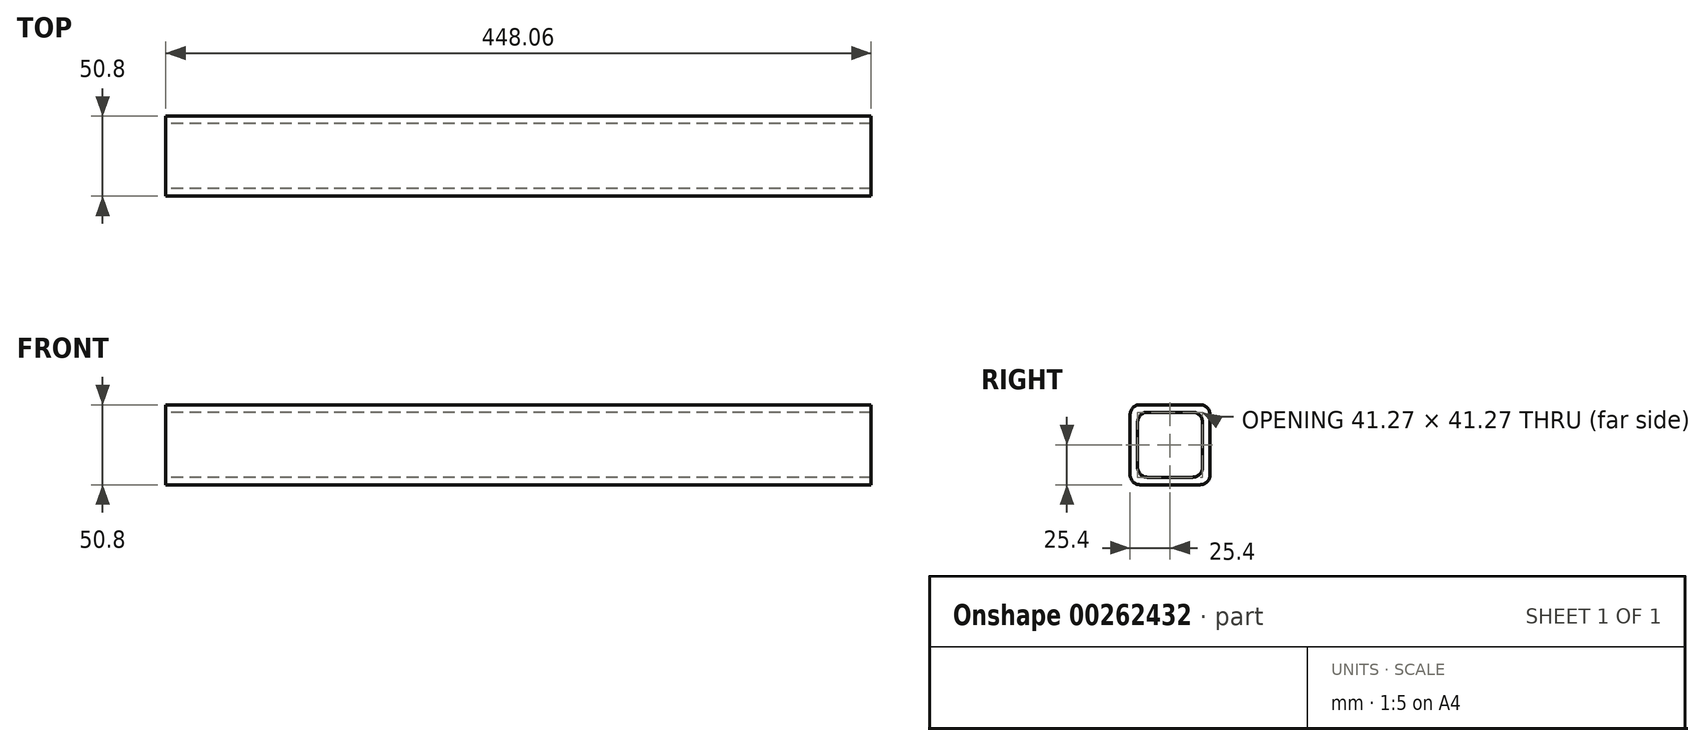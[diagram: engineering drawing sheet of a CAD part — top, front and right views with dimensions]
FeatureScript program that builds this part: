
annotation { "Feature Type Name" : "Feature", "Feature Type Description" : "" }
export const myFeature = defineFeature(function(context is Context, id is Id, definition is map)
    precondition{}
    {
        {
            var Q0;
            Q0=qCreatedBy(makeId("Right.planeOp"),FACE);
            var sketch = newSketch(context, id + "F0", { "sketchPlane" : qUnion([Q0])});
            skLineSegment(sketch, "E0.bottom", {"start": v(19.05, 25.4) * mm, "end": v(-19.05, 25.4) * mm});
            skLineSegment(sketch, "E0.top", {"start": v(19.05, -25.4) * mm, "end": v(-19.05, -25.4) * mm});
            skLineSegment(sketch, "E0.left", {"start": v(25.4, 19.05) * mm, "end": v(25.4, -19.05) * mm});
            skLineSegment(sketch, "E0.right", {"start": v(-25.4, 19.05) * mm, "end": v(-25.4, -19.05) * mm});
            skPoint(sketch, "E0.middle", {"position": v(0, 0) * mm});
            skLineSegment(sketch, "E1.bottom", {"start": v(14.29, 20.64) * mm, "end": v(-14.29, 20.64) * mm});
            skLineSegment(sketch, "E1.top", {"start": v(14.29, -20.64) * mm, "end": v(-14.29, -20.64) * mm});
            skLineSegment(sketch, "E1.left", {"start": v(20.64, 14.29) * mm, "end": v(20.64, -14.29) * mm});
            skLineSegment(sketch, "E1.right", {"start": v(-20.64, 14.29) * mm, "end": v(-20.64, -14.29) * mm});
            skPoint(sketch, "E2.visualSharp", {"position": v(-25.4, 25.4) * mm});
            skArc(sketch, "E2.filletArc", {"start": v(-19.05, 25.4) * mm, "mid": v(-23.54, 23.54) * mm, "end": v(-25.4, 19.05) * mm});
            skPoint(sketch, "E3.visualSharp", {"position": v(-20.64, 20.64) * mm});
            skArc(sketch, "E3.filletArc", {"start": v(-14.29, 20.64) * mm, "mid": v(-18.78, 18.78) * mm, "end": v(-20.64, 14.29) * mm});
            skPoint(sketch, "E4.visualSharp", {"position": v(-25.4, -25.4) * mm});
            skArc(sketch, "E4.filletArc", {"start": v(-25.4, -19.05) * mm, "mid": v(-23.54, -23.54) * mm, "end": v(-19.05, -25.4) * mm});
            skPoint(sketch, "E5.visualSharp", {"position": v(-20.64, -20.64) * mm});
            skArc(sketch, "E5.filletArc", {"start": v(-20.64, -14.29) * mm, "mid": v(-18.78, -18.78) * mm, "end": v(-14.29, -20.64) * mm});
            skPoint(sketch, "E6.visualSharp", {"position": v(20.64, 20.64) * mm});
            skArc(sketch, "E6.filletArc", {"start": v(20.64, 14.29) * mm, "mid": v(18.78, 18.78) * mm, "end": v(14.29, 20.64) * mm});
            skPoint(sketch, "E7.visualSharp", {"position": v(25.4, 25.4) * mm});
            skArc(sketch, "E7.filletArc", {"start": v(25.4, 19.05) * mm, "mid": v(23.54, 23.54) * mm, "end": v(19.05, 25.4) * mm});
            skPoint(sketch, "E8.visualSharp", {"position": v(20.64, -20.64) * mm});
            skArc(sketch, "E8.filletArc", {"start": v(14.29, -20.64) * mm, "mid": v(18.78, -18.78) * mm, "end": v(20.64, -14.29) * mm});
            skPoint(sketch, "E9.visualSharp", {"position": v(25.4, -25.4) * mm});
            skArc(sketch, "E9.filletArc", {"start": v(19.05, -25.4) * mm, "mid": v(23.54, -23.54) * mm, "end": v(25.4, -19.05) * mm});
            skSolve(sketch);
        }
        {
            var Q0;
            Q0 = qSketchRegion(id + "F0", true);
            extrude(context, id + "F1", {"entities" : qUnion([Q0]), "depth" : 448.06 * mm});
        }
    });
